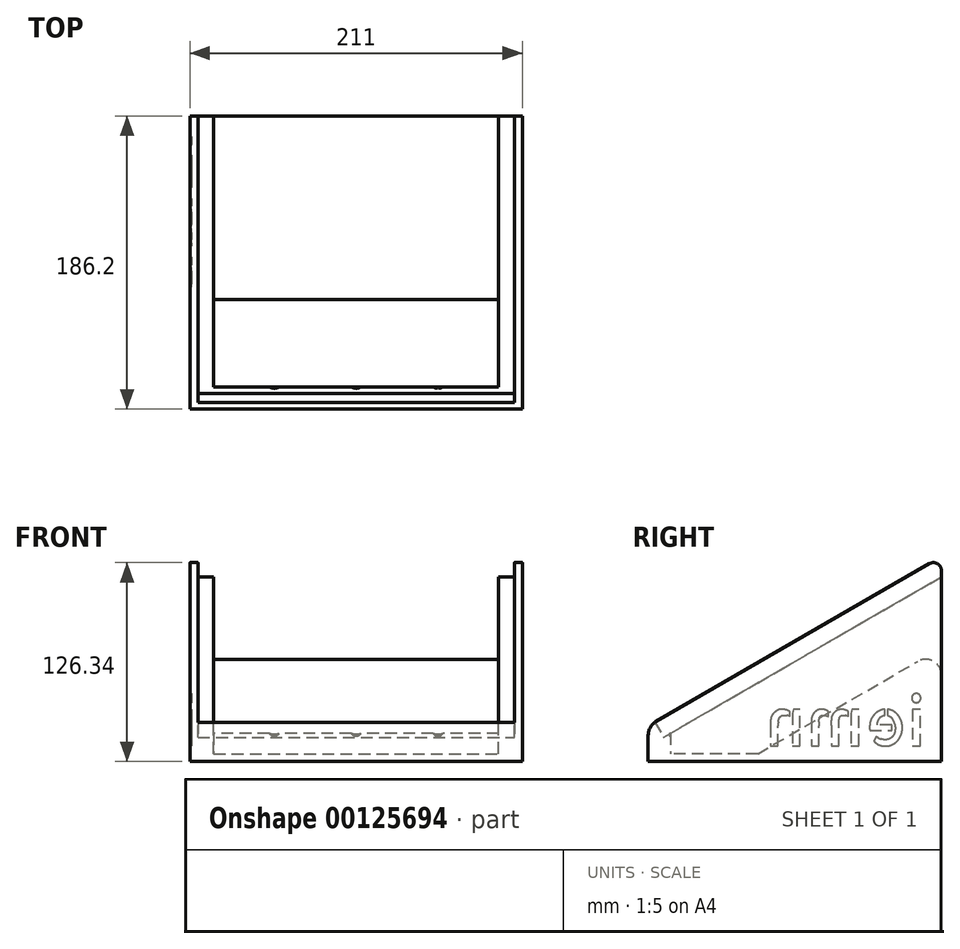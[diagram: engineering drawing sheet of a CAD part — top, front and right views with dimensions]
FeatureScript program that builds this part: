
annotation { "Feature Type Name" : "Feature", "Feature Type Description" : "" }
export const myFeature = defineFeature(function(context is Context, id is Id, definition is map)
    precondition{}
    {
        {
            var Q0;
            Q0=qCreatedBy(makeId("Right.planeOp"),FACE);
            var sketch = newSketch(context, id + "F0", { "sketchPlane" : qUnion([Q0])});
            skLineSegment(sketch, "E0", {"start": v(38.97, 22.5) * mm, "end": v(225.17, 130) * mm});
            skLineSegment(sketch, "E1", {"start": v(225.17, 130) * mm, "end": v(225.17, 0) * mm});
            skLineSegment(sketch, "E2", {"start": v(225.17, 0) * mm, "end": v(38.97, 0) * mm});
            skLineSegment(sketch, "E3", {"start": v(38.97, 22.5) * mm, "end": v(38.97, 0) * mm});
            skPoint(sketch, "E4.orphan", {"position": v(0, 0) * mm});
            skLineSegment(sketch, "E5", {"start": v(0, 0) * mm, "end": v(38.97, 22.5) * mm, "construction": true});
            skLineSegment(sketch, "E6", {"start": v(0, 0) * mm, "end": v(38.97, 0) * mm, "construction": true});
            skSolve(sketch);
        }
        {
            var Q0;
            Q0 = qSketchRegion(id + "F0", true);
            extrude(context, id + "F1", {"entities" : qUnion([Q0]), "depth" : 105.5 * mm, "hasSecondDirection" : true, "secondDirectionOppositeDirection" : true, "secondDirectionDepth" : 105.5 * mm});
        }
        {
            var Q0;
            Q0=makeQuery(id+"F1.opExtrude","SWEPT_FACE",FACE,{"disambiguationData":[OSD([sQuery(id+"F0.wireOp",EDGE,"E1")])]});
            var sketch = newSketch(context, id + "F2", { "sketchPlane" : qUnion([Q0])});
            skLineSegment(sketch, "E7.bottom", {"start": v(-90.5, 130) * mm, "end": v(90.5, 130) * mm});
            skLineSegment(sketch, "E7.top", {"start": v(-90.5, 0) * mm, "end": v(90.5, 0) * mm});
            skLineSegment(sketch, "E7.left", {"start": v(-90.5, 130) * mm, "end": v(-90.5, 0) * mm});
            skLineSegment(sketch, "E8", {"start": v(90.5, 130) * mm, "end": v(90.5, 0) * mm});
            skSolve(sketch);
        }
        {
            var Q0;
            Q0 = qSketchRegion(id + "F2", true);
            extrude(context, id + "F3", {"entities" : qUnion([Q0]), "operationType" : NewBodyOperationType.REMOVE, "oppositeDirection" : true, "depth" : 230 * mm});
        }
        {
            var Q0;
            {var subQ0=sQuery(id+"F0.wireOp",EDGE,"E0");var subQ1=sQuery(id+"F0.wireOp",EDGE,"E1");Q0=makeQuery(id+"F3.boolean.opBoolean","SPLIT",EDGE,{"disambiguationData":[TD([makeQuery(id+"F3.opExtrude","SWEPT_FACE",FACE,{"disambiguationData":[OSD([sQuery(id+"F2.wireOp",EDGE,"E7.left")])]})])],"derivedFrom":makeQuery(id+"F1.opExtrude","SWEPT_EDGE",EDGE,{"disambiguationData":[OSD([subQ0,subQ1])]})});}
            cPlane(context, id + "F4", {"entities" : qUnion([Q0]), "cplaneType" : CPlaneType.LINE_ANGLE, "offset" : 0 * mm, "angle" : 330 * degree, "width" : 150 * mm, "height" : 150 * mm});
        }
        {
            var Q0;
            Q0=qCreatedBy(id+"F4.planeOp",FACE);
            var sketch = newSketch(context, id + "F5", { "sketchPlane" : qUnion([Q0])});
            skLineSegment(sketch, "E9", {"start": v(90.5, 0) * mm, "end": v(100.5, 0) * mm});
            skLineSegment(sketch, "E10", {"start": v(100.5, 0) * mm, "end": v(100.5, -11) * mm});
            skLineSegment(sketch, "E11", {"start": v(100.5, -11) * mm, "end": v(90.5, -11) * mm});
            skLineSegment(sketch, "E12", {"start": v(0, 21.5) * mm, "end": v(0, -62.02) * mm, "construction": true});
            skLineSegment(sketch, "E13", {"start": v(90.5, 0) * mm, "end": v(90.5, -11) * mm});
            skLineSegment(sketch, "E14.MirrorCS", {"start": v(-90.5, 0) * mm, "end": v(-100.5, 0) * mm});
            skLineSegment(sketch, "E15.MirrorCS", {"start": v(-100.5, 0) * mm, "end": v(-100.5, -11) * mm});
            skLineSegment(sketch, "E16.MirrorCS", {"start": v(-100.5, -11) * mm, "end": v(-90.5, -11) * mm});
            skLineSegment(sketch, "E17.MirrorCS", {"start": v(-90.5, 0) * mm, "end": v(-90.5, -11) * mm});
            skSolve(sketch);
        }
        {
            var Q0;
            Q0=makeQuery(id+"F5.imprint","IMPRINT",FACE,{"disambiguationData":[TD([[makeQuery(id+"F5.imprint","IMPRINT",EDGE,{"derivedFrom":sQuery(id+"F5.wireOp",EDGE,"E9")}),-1.0]])]});
            var Q1;
            Q1=makeQuery(id+"F5.imprint","IMPRINT",FACE,{"disambiguationData":[TD([[makeQuery(id+"F5.imprint","IMPRINT",EDGE,{"derivedFrom":sQuery(id+"F5.wireOp",EDGE,"E14.MirrorCS")}),1.0]])]});
            extrude(context, id + "F6", {"entities" : qUnion([Q0, Q1]), "operationType" : NewBodyOperationType.REMOVE, "depth" : 210 * mm});
        }
        {
            var Q0;
            Q0=makeQuery(id+"F5LiILYsiGkCDB9_1.boolean.opBoolean","MERGE",FACE,{"derivedFrom":[makeQuery(id+"F1.opExtrude","CAP_FACE",FACE,{"disambiguationData":[OSD([sQuery(id+"F0.wireOp",EDGE,"E0"),sQuery(id+"F0.wireOp",EDGE,"E1"),sQuery(id+"F0.wireOp",EDGE,"E2"),sQuery(id+"F0.wireOp",EDGE,"E3")])],"isStart":false}),makeQuery(id+"F5LiILYsiGkCDB9_1.opExtrude","SWEPT_FACE",FACE,{"disambiguationData":[OSD([sQuery(id+"F20.wireOp",EDGE,"E37.right")])]})]});
            var sketch = newSketch(context, id + "F7", { "sketchPlane" : qUnion([Q0])});
            skLineSegment(sketch, "E18", {"start": v(100, 0) * mm, "end": v(225.17, 72.26) * mm});
            skLineSegment(sketch, "E19", {"start": v(225.17, 72.26) * mm, "end": v(225.17, 0) * mm});
            skLineSegment(sketch, "E20", {"start": v(220.17, 5) * mm, "end": v(220.17, 63.6) * mm, "construction": true});
            skLineSegment(sketch, "E21", {"start": v(220.17, 63.6) * mm, "end": v(118.66, 5) * mm, "construction": true});
            skLineSegment(sketch, "E22", {"start": v(100, 0) * mm, "end": v(110, 0) * mm});
            skLineSegment(sketch, "E23", {"start": v(220.17, 0) * mm, "end": v(225.17, 0) * mm});
            skLineSegment(sketch, "E24", {"start": v(100, 0) * mm, "end": v(225.17, 0) * mm});
            skLineSegment(sketch, "E25.0", {"start": v(118.66, 5) * mm, "end": v(220.17, 5) * mm, "construction": true});
            skSolve(sketch);
        }
        {
            var Q0;
            {var subQ4=sQuery(id+"F7.wireOp",EDGE,"E18");Q0=makeQuery(id+"F7.imprint","IMPRINT",FACE,{"disambiguationData":[TD([[makeQuery(id+"F7.imprint","IMPRINT",EDGE,{"derivedFrom":subQ4}),-1.0]])]});}
            var Q1;
            {var subQ3=sQuery(id+"F7.wireOp",EDGE,"Txo89btI-PvbI-ElAl-sVxU-Nita1zdl9piD");Q1=makeQuery(id+"F7.imprint","IMPRINT",FACE,{"disambiguationData":[TD([[makeQuery(id+"F7.imprint","IMPRINT",EDGE,{"derivedFrom":subQ3}),-1.0]])]});}
            extrude(context, id + "F8", {"entities" : qUnion([Q0, Q1]), "operationType" : NewBodyOperationType.ADD, "oppositeDirection" : true, "depth" : 210 * mm});
        }
        {
            var Q0;
            Q0=qCreatedBy(makeId("Top.planeOp"),FACE);
            var sketch = newSketch(context, id + "F9", { "sketchPlane" : qUnion([Q0])});
            skLineSegment(sketch, "E26.bottom", {"start": v(-140, 255.17) * mm, "end": v(140, 255.17) * mm});
            skLineSegment(sketch, "E26.top", {"start": v(-140, 225.17) * mm, "end": v(140, 225.17) * mm});
            skLineSegment(sketch, "E26.left", {"start": v(-140, 255.17) * mm, "end": v(-140, 225.17) * mm});
            skLineSegment(sketch, "E26.right", {"start": v(140, 255.17) * mm, "end": v(140, 225.17) * mm});
            skSolve(sketch);
        }
        {
            var Q0;
            Q0 = qSketchRegion(id + "F9", true);
            extrude(context, id + "F10", {"entities" : qUnion([Q0]), "operationType" : NewBodyOperationType.REMOVE, "depth" : 261.75 * mm});
        }
        {
            var Q0;
            {var subQ6=sQuery(id+"F5.wireOp",EDGE,"1e143367-0eed-4de3-a5ad-cce088774a1d0.MirrorCS");Q0=makeQuery(id+"F8.boolean.opBoolean","SPLIT",FACE,{"disambiguationData":[TD([makeQuery(id+"F1.opExtrude","SWEPT_FACE",FACE,{"disambiguationData":[OSD([sQuery(id+"F0.wireOp",EDGE,"E0")])]})])],"derivedFrom":makeQuery(id+"F6.boolean.opBoolean","MERGE",FACE,{"derivedFrom":[makeQuery(id+"F3.boolean.opBoolean","COPY",FACE,{"derivedFrom":makeQuery(id+"F3.opExtrude","SWEPT_FACE",FACE,{"disambiguationData":[OSD([sQuery(id+"F2.wireOp",EDGE,"E8")])]})}),makeQuery(id+"F6.opExtrude","SWEPT_FACE",FACE,{"disambiguationData":[OSD([subQ6])]})]})});}
            var sketch = newSketch(context, id + "F11", { "sketchPlane" : qUnion([Q0])});
            skLineSegment(sketch, "E27", {"start": v(38.97, 22.5) * mm, "end": v(38.97, 0) * mm});
            skLineSegment(sketch, "E28", {"start": v(53.13, 0) * mm, "end": v(38.97, 0) * mm});
            skLineSegment(sketch, "E29", {"start": v(43.3, 25) * mm, "end": v(48.8, 15.47) * mm});
            skLineSegment(sketch, "E30", {"start": v(38.97, 22.5) * mm, "end": v(43.3, 25) * mm});
            skLineSegment(sketch, "E31", {"start": v(53.13, 17.97) * mm, "end": v(48.8, 15.47) * mm});
            skLineSegment(sketch, "E32", {"start": v(53.13, 17.97) * mm, "end": v(53.13, 0) * mm});
            skSolve(sketch);
        }
        {
            var Q0;
            Q0 = qSketchRegion(id + "F11", true);
            extrude(context, id + "F12", {"entities" : qUnion([Q0]), "operationType" : NewBodyOperationType.ADD, "depth" : 190 * mm});
        }
        {
            var Q0;
            Q0=makeQuery(id+"F1.opExtrude","CAP_FACE",FACE,{"disambiguationData":[OSD([sQuery(id+"F0.wireOp",EDGE,"E0"),sQuery(id+"F0.wireOp",EDGE,"E1"),sQuery(id+"F0.wireOp",EDGE,"E2")])],"isStart":true});
            var sketch = newSketch(context, id + "F13", { "sketchPlane" : qUnion([Q0])});
            skText(sketch, "E33", { "text": "iemn", "fontName": "AllertaStencil-Regular.ttf"});
            const initialGuessF13  = {"E33": [-0.21517, 0.01, 1, 0, 0.03]};
            skSetInitialGuess(sketch, initialGuessF13);
            skSolve(sketch);
        }
        {
            var Q0;
            Q0 = qSketchRegion(id + "F13", true);
            extrude(context, id + "F14", {"entities" : qUnion([Q0]), "operationType" : NewBodyOperationType.REMOVE, "oppositeDirection" : true, "depth" : 1 * mm});
        }
        {
            var Q0;
            {var subQ0=sQuery(id+"F0.wireOp",EDGE,"E0");var subQ1=sQuery(id+"F0.wireOp",EDGE,"E1");Q0=makeQuery(id+"F10.boolean.opBoolean","MERGE",EDGE,{"derivedFrom":[makeQuery(id+"F3.boolean.opBoolean","SPLIT",EDGE,{"disambiguationData":[TD([makeQuery(id+"F3.opExtrude","SWEPT_FACE",FACE,{"disambiguationData":[OSD([sQuery(id+"F2.wireOp",EDGE,"E7.left")])]})])],"derivedFrom":makeQuery(id+"F1.opExtrude","SWEPT_EDGE",EDGE,{"disambiguationData":[OSD([subQ0,subQ1])]})}),makeQuery(id+"F6.opExtrude","CAP_EDGE",EDGE,{"disambiguationData":[OSD([sQuery(id+"F5.wireOp",EDGE,"YftVb2uO-JKCj-4i0A-fwTr-itcp59TeQrzk.top")])],"isStart":true})]});}
            var Q1;
            {var subQ0=sQuery(id+"F0.wireOp",EDGE,"E1");var subQ1=sQuery(id+"F0.wireOp",EDGE,"E0");Q1=makeQuery(id+"F10.boolean.opBoolean","MERGE",EDGE,{"derivedFrom":[makeQuery(id+"F3.boolean.opBoolean","SPLIT",EDGE,{"disambiguationData":[TD([makeQuery(id+"F5LiILYsiGkCDB9_1.opExtrude","SWEPT_FACE",FACE,{"disambiguationData":[OSD([sQuery(id+"F20.wireOp",EDGE,"iXoTAtqL-46hs-OJW5-uACF-wR98uR8jGWd5.right")])]})])],"derivedFrom":makeQuery(id+"F1.opExtrude","SWEPT_EDGE",EDGE,{"disambiguationData":[OSD([subQ1,subQ0])]})}),makeQuery(id+"F6.opExtrude","CAP_EDGE",EDGE,{"disambiguationData":[OSD([sQuery(id+"F5.wireOp",EDGE,"33e05e6d-aa6e-46c1-81ee-74ff33667d9d0.MirrorCS")])],"isStart":true})]});}
            var Q2;
            Q2=makeQuery(id+"F8.opExtrude","SWEPT_EDGE",EDGE,{"disambiguationData":[OSD([sQuery(id+"F7.wireOp",EDGE,"E20"),sQuery(id+"F7.wireOp",EDGE,"E21")])]});
            var Q3;
            {var subQ0=sQuery(id+"F0.wireOp",EDGE,"E0");var subQ1=sQuery(id+"F0.wireOp",EDGE,"E1");Q3=makeQuery(id+"F3.boolean.opBoolean","SPLIT",EDGE,{"disambiguationData":[TD([makeQuery(id+"F3.opExtrude","SWEPT_FACE",FACE,{"disambiguationData":[OSD([sQuery(id+"F2.wireOp",EDGE,"E8")])]})])],"derivedFrom":makeQuery(id+"F1.opExtrude","SWEPT_EDGE",EDGE,{"disambiguationData":[OSD([subQ0,subQ1])]})});}
            fillet(context, id + "F15", {"entities" : qUnion([Q0, Q1, Q2, Q3]), "radius" : 5 * mm, "tangentPropagation" : true, "allowEdgeOverflow" : false});
        }
        {
            var Q0;
            {var subQ0=sQuery(id+"F0.wireOp",EDGE,"E0");var subQ2=sQuery(id+"F0.wireOp",EDGE,"E3");var subQ6=makeQuery(id+"F1.opExtrude","SWEPT_EDGE",EDGE,{"disambiguationData":[OSD([subQ0,subQ2])]});Q0=makeQuery(id+"F12.boolean.opBoolean","MERGE",EDGE,{"derivedFrom":[makeQuery(id+"F3.boolean.opBoolean","SPLIT",EDGE,{"disambiguationData":[TD([makeQuery(id+"F3.opExtrude","SWEPT_FACE",FACE,{"disambiguationData":[OSD([sQuery(id+"F2.wireOp",EDGE,"E8")])]})])],"derivedFrom":subQ6}),makeQuery(id+"F3.boolean.opBoolean","SPLIT",EDGE,{"disambiguationData":[TD([makeQuery(id+"F3.opExtrude","SWEPT_FACE",FACE,{"disambiguationData":[OSD([sQuery(id+"F2.wireOp",EDGE,"E7.left")])]})])],"derivedFrom":subQ6}),makeQuery(id+"F12.opExtrude","SWEPT_EDGE",EDGE,{"disambiguationData":[OSD([sQuery(id+"F11.wireOp",EDGE,"E27"),sQuery(id+"F11.wireOp",EDGE,"E30")])]})]});}
            fillet(context, id + "F16", {"entities" : qUnion([Q0]), "radius" : 10 * mm, "tangentPropagation" : true, "allowEdgeOverflow" : false});
        }
        {
            var Q0;
            Q0=makeQuery(id+"F8.opExtrude","SWEPT_EDGE",EDGE,{"disambiguationData":[OSD([sQuery(id+"F0.wireOp",EDGE,"E1"),sQuery(id+"F20.wireOp",EDGE,"E39.MirrorCS"),sQuery(id+"F20.wireOp",EDGE,"602d57a4-2f6a-4474-a667-b8c03bd0cbda0.MirrorCS"),sQuery(id+"F7.wireOp",EDGE,"E18"),sQuery(id+"F7.wireOp",EDGE,"E19")])]});
            fillet(context, id + "F17", {"entities" : qUnion([Q0]), "radius" : 10 * mm, "tangentPropagation" : true, "allowEdgeOverflow" : false});
        }
        {
            var Q0;
            {var subQ3=sQuery(id+"F0.wireOp",EDGE,"E0");var subQ6=makeQuery(id+"F1.opExtrude","SWEPT_FACE",FACE,{"disambiguationData":[OSD([subQ3])]});Q0=makeQuery(id+"F12.boolean.opBoolean","MERGE",FACE,{"derivedFrom":[makeQuery(id+"F3.boolean.opBoolean","SPLIT",FACE,{"disambiguationData":[TD([makeQuery(id+"F3.opExtrude","SWEPT_FACE",FACE,{"disambiguationData":[OSD([sQuery(id+"F2.wireOp",EDGE,"E8")])]})])],"derivedFrom":subQ6}),makeQuery(id+"F3.boolean.opBoolean","SPLIT",FACE,{"disambiguationData":[TD([makeQuery(id+"F3.opExtrude","SWEPT_FACE",FACE,{"disambiguationData":[OSD([sQuery(id+"F2.wireOp",EDGE,"E7.left")])]})])],"derivedFrom":subQ6}),makeQuery(id+"F12.opExtrude","SWEPT_FACE",FACE,{"disambiguationData":[OSD([sQuery(id+"F11.wireOp",EDGE,"E30")])]})]});}
            var sketch = newSketch(context, id + "F18", { "sketchPlane" : qUnion([Q0])});
            skCircle(sketch, "E34", {"center": v(-52, 58.95) * mm, "radius": 5 * mm});
            skCircle(sketch, "E35.1.0.0", {"center": v(0, 58.95) * mm, "radius": 5 * mm});
            skCircle(sketch, "E35.2.0.0", {"center": v(52, 58.95) * mm, "radius": 5 * mm});
            skLineSegment(sketch, "E35.direction1", {"start": v(-52, 58.95) * mm, "end": v(0, 58.95) * mm, "construction": true});
            skLineSegment(sketch, "E36.bottom", {"start": v(-100, 50.77) * mm, "end": v(100, 50.77) * mm, "construction": true});
            skLineSegment(sketch, "E36.top", {"start": v(-100, 250.77) * mm, "end": v(100, 250.77) * mm, "construction": true});
            skLineSegment(sketch, "E36.left", {"start": v(-100, 50.77) * mm, "end": v(-100, 250.77) * mm, "construction": true});
            skLineSegment(sketch, "E36.right", {"start": v(100, 50.77) * mm, "end": v(100, 250.77) * mm, "construction": true});
            skSolve(sketch);
        }
        {
            var Q0;
            Q0 = qSketchRegion(id + "F18", true);
            extrude(context, id + "F19", {"entities" : qUnion([Q0]), "operationType" : NewBodyOperationType.REMOVE, "oppositeDirection" : true, "depth" : 25 * mm});
        }
        {
            var Q0;
            Q0=qCreatedBy(makeId("Top.planeOp"),FACE);
            var sketch = newSketch(context, id + "F20", { "sketchPlane" : qUnion([Q0])});
            skLineSegment(sketch, "E37.bottom", {"start": v(-105.5, 38.97) * mm, "end": v(105.5, 38.97) * mm});
            skLineSegment(sketch, "E37.left", {"start": v(-105.5, 38.97) * mm, "end": v(-105.5, 110.97) * mm});
            skLineSegment(sketch, "E37.right", {"start": v(105.5, 38.97) * mm, "end": v(105.5, 110.97) * mm});
            skLineSegment(sketch, "E38", {"start": v(0, 38.97) * mm, "end": v(0, 269.9) * mm, "construction": true});
            skPoint(sketch, "E38.endSnap0", {"position": v(0, 110.97) * mm});
            skPoint(sketch, "E39.MirrorCS.start.orphan", {"position": v(105.5, 110.97) * mm});
            skLineSegment(sketch, "E40", {"start": v(105.5, 110.97) * mm, "end": v(-105.5, 110.97) * mm});
            skSolve(sketch);
        }
        {
            var Q0;
            Q0 = qSketchRegion(id + "F20", true);
            extrude(context, id + "F21", {"entities" : qUnion([Q0]), "operationType" : NewBodyOperationType.ADD, "depth" : 5 * mm});
        }
    });
